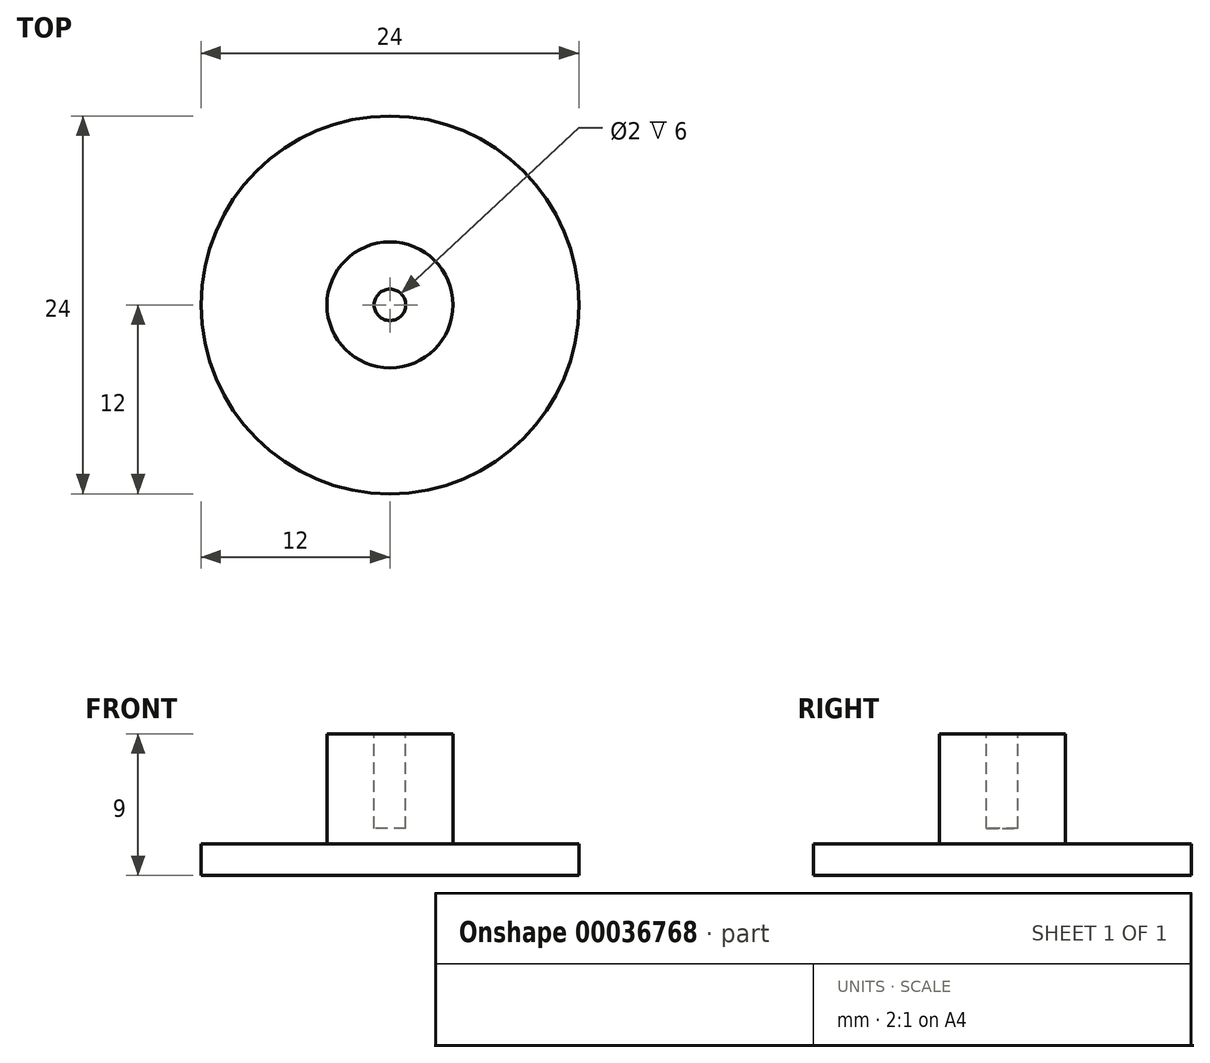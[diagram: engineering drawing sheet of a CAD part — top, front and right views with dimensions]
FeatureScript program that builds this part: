
annotation { "Feature Type Name" : "Feature", "Feature Type Description" : "" }
export const myFeature = defineFeature(function(context is Context, id is Id, definition is map)
    precondition{}
    {
        {
            var Q0;
            Q0=qCreatedBy(makeId("Front.planeOp"),FACE);
            var sketch = newSketch(context, id + "F0", { "sketchPlane" : qUnion([Q0])});
            skLineSegment(sketch, "E0", {"start": v(0, 0) * mm, "end": v(-12, 0) * mm});
            skLineSegment(sketch, "E1", {"start": v(-12, 2) * mm, "end": v(-12, 0) * mm});
            skLineSegment(sketch, "E2", {"start": v(-12, 2) * mm, "end": v(-4, 2) * mm});
            skLineSegment(sketch, "E3", {"start": v(-4, 2) * mm, "end": v(-4, 9) * mm});
            skLineSegment(sketch, "E4", {"start": v(-4, 9) * mm, "end": v(-1, 9) * mm});
            skLineSegment(sketch, "E5", {"start": v(-1, 9) * mm, "end": v(-1, 3) * mm});
            skLineSegment(sketch, "E6", {"start": v(-1, 3) * mm, "end": v(0, 3) * mm});
            skLineSegment(sketch, "E7", {"start": v(0, 3) * mm, "end": v(0, 0) * mm});
            skSolve(sketch);
        }
        {
            var Q0;
            Q0=makeQuery(id+"F0.imprint","IMPRINT",FACE,{"disambiguationData":[TD([[makeQuery(id+"F0.imprint","IMPRINT",EDGE,{"derivedFrom":sQuery(id+"F0.wireOp",EDGE,"E0")}),-1.0]])]});
            var Q1;
            Q1=sQuery(id+"F0.wireOp",EDGE,"E7");
            revolve(context, id + "F1", {"entities" : qUnion([Q0]), "axis" : qUnion([Q1]), "revolveType" : RevolveType.FULL});
        }
    });
